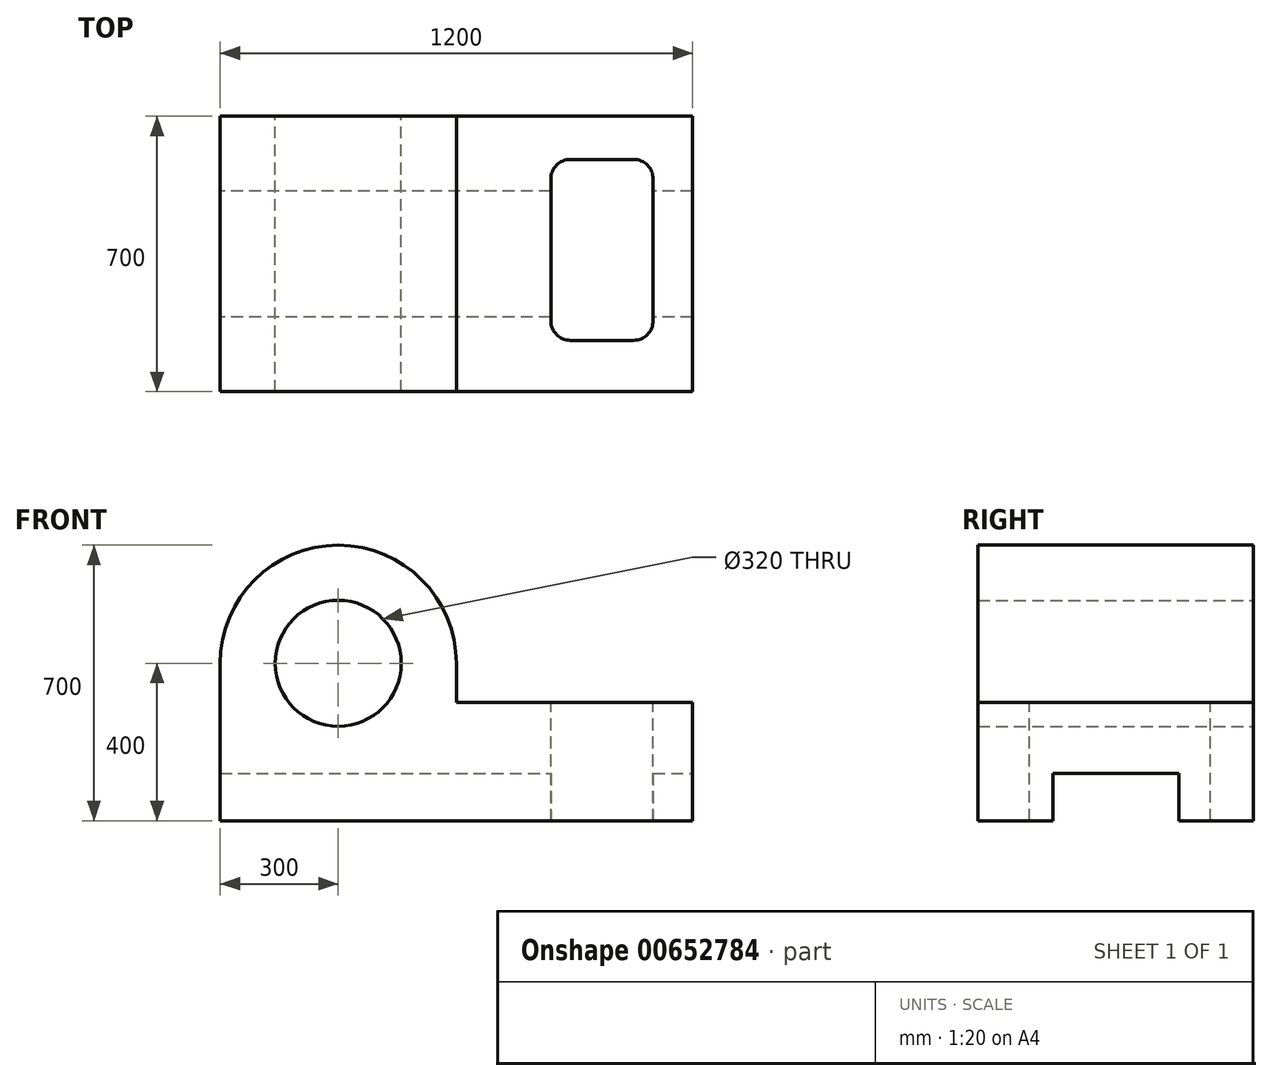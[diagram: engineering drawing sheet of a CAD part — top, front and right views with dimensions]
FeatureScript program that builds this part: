
annotation { "Feature Type Name" : "Feature", "Feature Type Description" : "" }
export const myFeature = defineFeature(function(context is Context, id is Id, definition is map)
    precondition{}
    {
        {
            var Q0;
            Q0=qCreatedBy(makeId("Front.planeOp"),FACE);
            var sketch = newSketch(context, id + "F0", { "sketchPlane" : qUnion([Q0])});
            skLineSegment(sketch, "E0.bottom", {"start": v(-600, -150) * mm, "end": v(600, -150) * mm});
            skLineSegment(sketch, "E0.top", {"start": v(-600, 150) * mm, "end": v(600, 150) * mm});
            skLineSegment(sketch, "E0.left", {"start": v(-600, -150) * mm, "end": v(-600, 150) * mm});
            skLineSegment(sketch, "E0.right", {"start": v(600, -150) * mm, "end": v(600, 150) * mm});
            skPoint(sketch, "E0.middle", {"position": v(0, 0) * mm});
            skSolve(sketch);
        }
        {
            var Q0;
            Q0 = qSketchRegion(id + "F0", true);
            extrude(context, id + "F1", {"entities" : qUnion([Q0]), "depth" : 700 * mm, "offsetDistance" : 25 * mm});
        }
        {
            var Q0;
            Q0=makeQuery(id+"F1.opExtrude","CAP_FACE",FACE,{"disambiguationData":[OSD([sQuery(id+"F0.wireOp",EDGE,"E0.bottom"),sQuery(id+"F0.wireOp",EDGE,"E0.top"),sQuery(id+"F0.wireOp",EDGE,"E0.left"),sQuery(id+"F0.wireOp",EDGE,"E0.right")])],"isStart":true});
            var sketch = newSketch(context, id + "F2", { "sketchPlane" : qUnion([Q0])});
            skLineSegment(sketch, "E1.bottom", {"start": v(600, 150) * mm, "end": v(0, 150) * mm});
            skLineSegment(sketch, "E1.top", {"start": v(600, 250) * mm, "end": v(0, 250) * mm});
            skLineSegment(sketch, "E1.left", {"start": v(600, 150) * mm, "end": v(600, 250) * mm});
            skLineSegment(sketch, "E1.right", {"start": v(0, 150) * mm, "end": v(0, 250) * mm});
            skArc(sketch, "E2", {"start": v(600, 250) * mm, "mid": v(300, 550) * mm, "end": v(0, 250) * mm});
            skSolve(sketch);
        }
        {
            var Q0;
            Q0 = qSketchRegion(id + "F2", true);
            extrude(context, id + "F3", {"entities" : qUnion([Q0]), "operationType" : NewBodyOperationType.ADD, "oppositeDirection" : true, "depth" : 700 * mm, "offsetDistance" : 25 * mm});
        }
        {
            var Q0;
            Q0=makeQuery(id+"F3.boolean.opBoolean","MERGE",FACE,{"derivedFrom":[makeQuery(id+"F1.opExtrude","CAP_FACE",FACE,{"disambiguationData":[OSD([sQuery(id+"F0.wireOp",EDGE,"E0.bottom"),sQuery(id+"F0.wireOp",EDGE,"E0.top"),sQuery(id+"F0.wireOp",EDGE,"E0.left"),sQuery(id+"F0.wireOp",EDGE,"E0.right")])],"isStart":true}),makeQuery(id+"F3.opExtrude","CAP_FACE",FACE,{"disambiguationData":[OSD([sQuery(id+"F2.wireOp",EDGE,"E1.bottom"),sQuery(id+"F2.wireOp",EDGE,"E1.left"),sQuery(id+"F2.wireOp",EDGE,"E1.right"),sQuery(id+"F2.wireOp",EDGE,"E2")])],"isStart":true})]});
            var sketch = newSketch(context, id + "F4", { "sketchPlane" : qUnion([Q0])});
            skCircle(sketch, "E3", {"center": v(300, 250) * mm, "radius": 160 * mm});
            skSolve(sketch);
        }
        {
            var Q0;
            Q0 = qSketchRegion(id + "F4", true);
            extrude(context, id + "F5", {"entities" : qUnion([Q0]), "operationType" : NewBodyOperationType.REMOVE, "endBound" : BoundingType.THROUGH_ALL, "oppositeDirection" : true, "depth" : 800 * mm, "offsetDistance" : 25 * mm});
        }
        {
            var Q0;
            Q0=makeQuery(id+"F1.opExtrude","SWEPT_FACE",FACE,{"disambiguationData":[OSD([sQuery(id+"F0.wireOp",EDGE,"E0.top")])]});
            var sketch = newSketch(context, id + "F6", { "sketchPlane" : qUnion([Q0])});
            skLineSegment(sketch, "E4.bottom", {"start": v(290, -109.62) * mm, "end": v(450, -109.62) * mm});
            skLineSegment(sketch, "E4.top", {"start": v(290, -569.62) * mm, "end": v(450, -569.62) * mm});
            skLineSegment(sketch, "E4.left", {"start": v(240, -159.62) * mm, "end": v(240, -519.62) * mm});
            skLineSegment(sketch, "E4.right", {"start": v(500, -159.62) * mm, "end": v(500, -519.62) * mm});
            skPoint(sketch, "E5.visualSharp", {"position": v(240, -109.62) * mm});
            skArc(sketch, "E5.filletArc", {"start": v(290, -109.62) * mm, "mid": v(254.64, -124.26) * mm, "end": v(240, -159.62) * mm});
            skPoint(sketch, "E6.visualSharp", {"position": v(500, -109.62) * mm});
            skArc(sketch, "E6.filletArc", {"start": v(500, -159.62) * mm, "mid": v(485.36, -124.26) * mm, "end": v(450, -109.62) * mm});
            skPoint(sketch, "E7.visualSharp", {"position": v(500, -569.62) * mm});
            skArc(sketch, "E7.filletArc", {"start": v(450, -569.62) * mm, "mid": v(485.36, -554.97) * mm, "end": v(500, -519.62) * mm});
            skPoint(sketch, "E8.visualSharp", {"position": v(240, -569.62) * mm});
            skArc(sketch, "E8.filletArc", {"start": v(240, -519.62) * mm, "mid": v(254.64, -554.97) * mm, "end": v(290, -569.62) * mm});
            skSolve(sketch);
        }
        {
            var Q0;
            Q0 = qSketchRegion(id + "F6", true);
            extrude(context, id + "F7", {"entities" : qUnion([Q0]), "operationType" : NewBodyOperationType.REMOVE, "endBound" : BoundingType.THROUGH_ALL, "oppositeDirection" : true, "depth" : 500 * mm, "offsetDistance" : 25 * mm});
        }
        {
            var Q0;
            Q0=makeQuery(id+"F1.opExtrude","SWEPT_FACE",FACE,{"disambiguationData":[OSD([sQuery(id+"F0.wireOp",EDGE,"E0.right")])]});
            var sketch = newSketch(context, id + "F8", { "sketchPlane" : qUnion([Q0])});
            skLineSegment(sketch, "E9.bottom", {"start": v(-510, -270) * mm, "end": v(-190, -270) * mm});
            skLineSegment(sketch, "E9.top", {"start": v(-510, -30) * mm, "end": v(-190, -30) * mm});
            skLineSegment(sketch, "E9.left", {"start": v(-510, -270) * mm, "end": v(-510, -30) * mm});
            skLineSegment(sketch, "E9.right", {"start": v(-190, -270) * mm, "end": v(-190, -30) * mm});
            skPoint(sketch, "E9.middle", {"position": v(-350, -150) * mm});
            skSolve(sketch);
        }
        {
            var Q0;
            Q0 = qSketchRegion(id + "F8", true);
            extrude(context, id + "F9", {"entities" : qUnion([Q0]), "operationType" : NewBodyOperationType.REMOVE, "endBound" : BoundingType.THROUGH_ALL, "oppositeDirection" : true, "depth" : 25 * mm, "offsetDistance" : 25 * mm});
        }
    });
